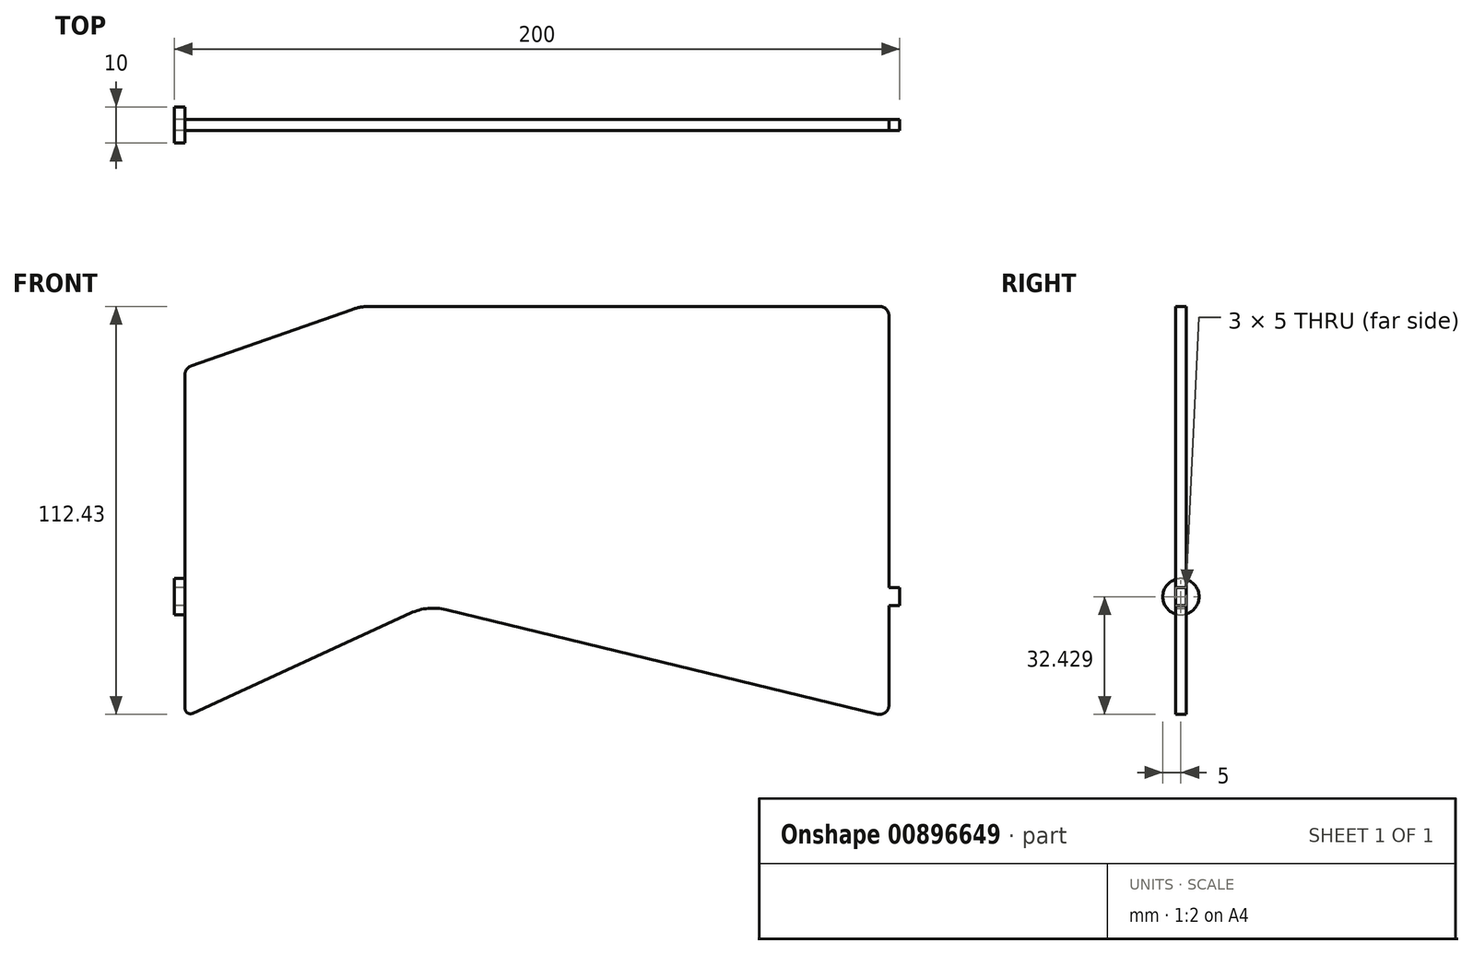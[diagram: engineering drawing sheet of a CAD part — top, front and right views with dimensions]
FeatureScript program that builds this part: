
annotation { "Feature Type Name" : "Feature", "Feature Type Description" : "" }
export const myFeature = defineFeature(function(context is Context, id is Id, definition is map)
    precondition{}
    {
        {
            assignVariable(context, id + "F0", {"name" : "thick", "anyValue" : 3 * mm});
        }
        {
            var Q0;
            Q0=qCreatedBy(makeId("Front.planeOp"),FACE);
            var sketch = newSketch(context, id + "F1", { "sketchPlane" : qUnion([Q0])});
            skLineSegment(sketch, "E0", {"start": v(-48.35, 94.36) * mm, "end": v(-48.35, 2.34) * mm});
            skLineSegment(sketch, "E1", {"start": v(-46.22, 0.98) * mm, "end": v(13.84, 28.58) * mm});
            skLineSegment(sketch, "E2", {"start": v(23.63, 29.53) * mm, "end": v(142.56, 0.75) * mm});
            skLineSegment(sketch, "E3", {"start": v(145.65, 3.18) * mm, "end": v(145.65, 110.6) * mm});
            skLineSegment(sketch, "E4", {"start": v(143.15, 113.1) * mm, "end": v(2.56, 113.1) * mm});
            skLineSegment(sketch, "E5", {"start": v(-2.41, 112.26) * mm, "end": v(-46.68, 96.72) * mm});
            skLineSegment(sketch, "E6", {"start": v(-48.35, 33.1) * mm, "end": v(145.65, 33.1) * mm, "construction": true});
            skLineSegment(sketch, "E7.bottom", {"start": v(-45.35, 30.6) * mm, "end": v(-51.35, 30.6) * mm});
            skLineSegment(sketch, "E7.top", {"start": v(-45.35, 35.6) * mm, "end": v(-51.35, 35.6) * mm});
            skLineSegment(sketch, "E7.left", {"start": v(-45.35, 30.6) * mm, "end": v(-45.35, 35.6) * mm});
            skLineSegment(sketch, "E7.right", {"start": v(-51.35, 30.6) * mm, "end": v(-51.35, 35.6) * mm});
            skPoint(sketch, "E7.middle", {"position": v(-48.35, 33.1) * mm});
            skLineSegment(sketch, "E8.bottom", {"start": v(148.65, 30.6) * mm, "end": v(142.65, 30.6) * mm});
            skLineSegment(sketch, "E8.top", {"start": v(148.65, 35.6) * mm, "end": v(142.65, 35.6) * mm});
            skLineSegment(sketch, "E8.left", {"start": v(148.65, 30.6) * mm, "end": v(148.65, 35.6) * mm});
            skLineSegment(sketch, "E8.right", {"start": v(142.65, 30.6) * mm, "end": v(142.65, 35.6) * mm});
            skPoint(sketch, "E8.middle", {"position": v(145.65, 33.1) * mm});
            skPoint(sketch, "E9.visualSharp", {"position": v(18.57, 30.76) * mm});
            skArc(sketch, "E9.filletArc", {"start": v(23.63, 29.53) * mm, "mid": v(18.66, 29.88) * mm, "end": v(13.84, 28.58) * mm});
            skPoint(sketch, "E10.visualSharp", {"position": v(0, 113.1) * mm});
            skArc(sketch, "E10.filletArc", {"start": v(2.56, 113.1) * mm, "mid": v(0.04, 112.9) * mm, "end": v(-2.41, 112.26) * mm});
            skPoint(sketch, "E11.visualSharp", {"position": v(-48.35, 0) * mm});
            skArc(sketch, "E11.filletArc", {"start": v(-48.35, 2.34) * mm, "mid": v(-47.66, 1.08) * mm, "end": v(-46.22, 0.98) * mm});
            skPoint(sketch, "E12.visualSharp", {"position": v(145.65, 113.1) * mm});
            skArc(sketch, "E12.filletArc", {"start": v(145.65, 110.6) * mm, "mid": v(144.92, 112.38) * mm, "end": v(143.15, 113.1) * mm});
            skPoint(sketch, "E13.visualSharp", {"position": v(145.65, 0) * mm});
            skArc(sketch, "E13.filletArc", {"start": v(142.56, 0.75) * mm, "mid": v(144.7, 1.21) * mm, "end": v(145.65, 3.18) * mm});
            skPoint(sketch, "E14.visualSharp", {"position": v(-48.35, 96.13) * mm});
            skArc(sketch, "E14.filletArc", {"start": v(-46.68, 96.72) * mm, "mid": v(-47.89, 95.8) * mm, "end": v(-48.35, 94.36) * mm});
            skSolve(sketch);
        }
        {
            var Q0;
            Q0 = qSketchRegion(id + "F1", true);
            extrude(context, id + "F2", {"entities" : qUnion([Q0]), "depth" : getVariable(context, 'thick'), "offsetDistance" : 25 * mm});
        }
        {
            var Q0;
            Q0=makeQuery(id+"F2.opExtrude","SWEPT_FACE",FACE,{"disambiguationData":[OSD([sQuery(id+"F1.wireOp",EDGE,"E7.right")])]});
            var sketch = newSketch(context, id + "F3", { "sketchPlane" : qUnion([Q0])});
            skCircle(sketch, "E15", {"center": v(1.5, 33.1) * mm, "radius": 5 * mm});
            skPoint(sketch, "E15.centerSnap0", {"position": v(0, 33.1) * mm});
            skPoint(sketch, "E15.centerSnap1", {"position": v(1.5, 30.6) * mm});
            skLineSegment(sketch, "E16.0", {"start": v(3, 35.6) * mm, "end": v(0, 35.6) * mm});
            skLineSegment(sketch, "E16.1", {"start": v(3, 30.6) * mm, "end": v(3, 35.6) * mm});
            skLineSegment(sketch, "E16.2", {"start": v(3, 30.6) * mm, "end": v(0, 30.6) * mm});
            skLineSegment(sketch, "E16.3", {"start": v(0, 30.6) * mm, "end": v(0, 35.6) * mm});
            skSolve(sketch);
        }
        {
            var Q0;
            Q0 = qSketchRegion(id + "F3", true);
            extrude(context, id + "F4", {"entities" : qUnion([Q0]), "oppositeDirection" : true, "depth" : getVariable(context, 'thick'), "offsetDistance" : 25 * mm});
        }
    });
